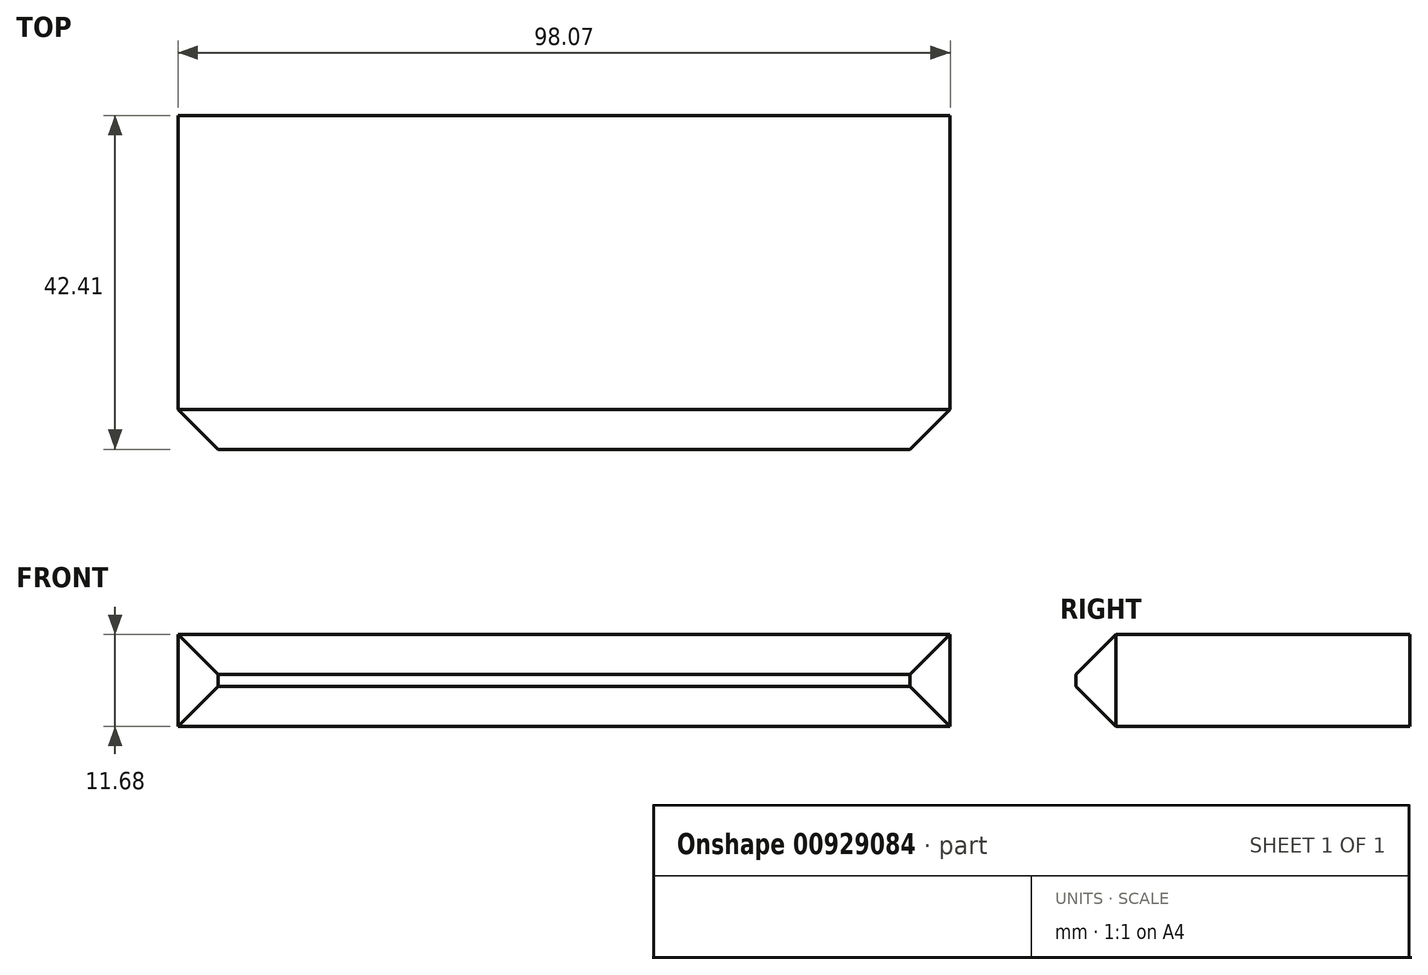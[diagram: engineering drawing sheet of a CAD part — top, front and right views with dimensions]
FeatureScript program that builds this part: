
annotation { "Feature Type Name" : "Feature", "Feature Type Description" : "" }
export const myFeature = defineFeature(function(context is Context, id is Id, definition is map)
    precondition{}
    {
        {
            var Q0;
            Q0=qCreatedBy(makeId("Top.planeOp"),FACE);
            var sketch = newSketch(context, id + "F0", { "sketchPlane" : qUnion([Q0])});
            skLineSegment(sketch, "E0.bottom", {"start": v(-57.3, -31.38) * mm, "end": v(40.77, -31.38) * mm});
            skLineSegment(sketch, "E0.top", {"start": v(-57.3, -73.8) * mm, "end": v(40.77, -73.8) * mm});
            skLineSegment(sketch, "E0.left", {"start": v(-57.3, -31.38) * mm, "end": v(-57.3, -73.8) * mm});
            skLineSegment(sketch, "E0.right", {"start": v(40.77, -31.38) * mm, "end": v(40.77, -73.8) * mm});
            skSolve(sketch);
        }
        {
            var Q0;
            Q0 = qSketchRegion(id + "F0", true);
            extrude(context, id + "F1", {"entities" : qUnion([Q0]), "depth" : 11.68 * mm, "offsetDistance" : 25.4 * mm});
        }
        {
            var Q0;
            Q0=makeQuery(id+"F1.opExtrude","SWEPT_FACE",FACE,{"disambiguationData":[OSD([sQuery(id+"F0.wireOp",EDGE,"E0.top")])]});
            var Q1;
            Q1=makeQuery(id+"F1.opExtrude","CAP_EDGE",EDGE,{"disambiguationData":[OSD([sQuery(id+"F0.wireOp",EDGE,"E0.top")])],"isStart":false});
            chamfer(context, id + "F2", {"entities" : qUnion([Q0, Q1]), "width" : 5.08 * mm, "tangentPropagation" : true});
        }
    });
